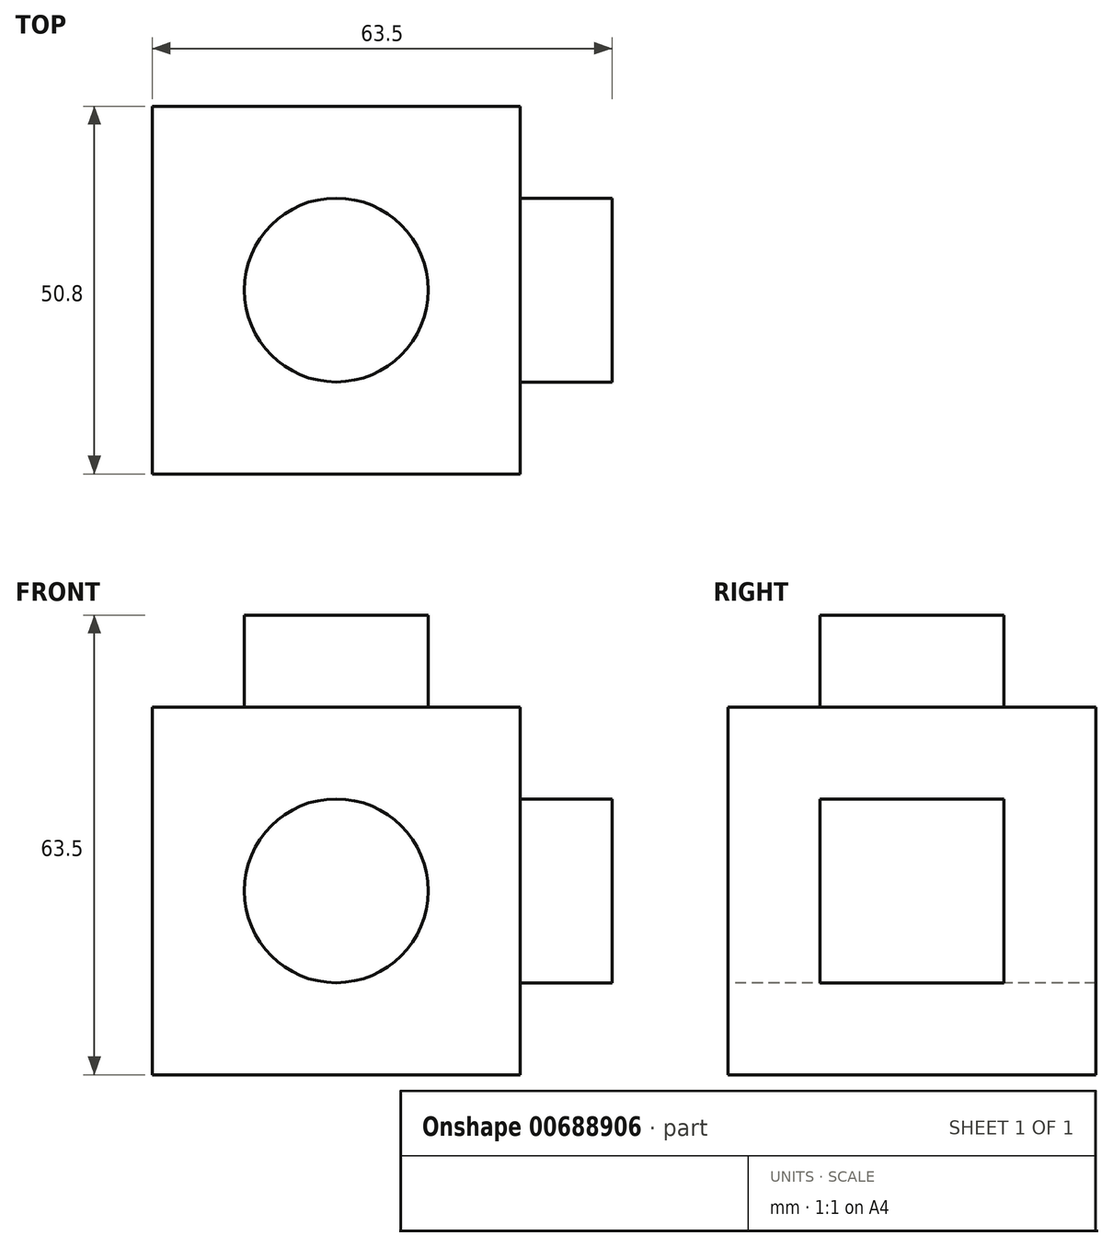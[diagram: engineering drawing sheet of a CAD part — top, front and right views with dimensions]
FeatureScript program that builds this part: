
annotation { "Feature Type Name" : "Feature", "Feature Type Description" : "" }
export const myFeature = defineFeature(function(context is Context, id is Id, definition is map)
    precondition{}
    {
        {
            var Q0;
            Q0=qCreatedBy(makeId("Front.planeOp"),FACE);
            var sketch = newSketch(context, id + "F0", { "sketchPlane" : qUnion([Q0])});
            skLineSegment(sketch, "E0.bottom", {"start": v(-18.43, 28.55) * mm, "end": v(32.37, 28.55) * mm});
            skLineSegment(sketch, "E0.top", {"start": v(-18.43, -22.25) * mm, "end": v(32.37, -22.25) * mm});
            skLineSegment(sketch, "E0.left", {"start": v(-18.43, 28.55) * mm, "end": v(-18.43, -22.25) * mm});
            skLineSegment(sketch, "E0.right", {"start": v(32.37, 28.55) * mm, "end": v(32.37, -22.25) * mm});
            skSolve(sketch);
        }
        {
            var Q0;
            Q0 = qSketchRegion(id + "F0", true);
            extrude(context, id + "F1", {"entities" : qUnion([Q0]), "depth" : 50.8 * mm, "offsetDistance" : 25.4 * mm});
        }
        {
            var Q0;
            Q0=makeQuery(id+"F1.opExtrude","CAP_FACE",FACE,{"disambiguationData":[OSD([sQuery(id+"F0.wireOp",EDGE,"E0.bottom"),sQuery(id+"F0.wireOp",EDGE,"E0.top"),sQuery(id+"F0.wireOp",EDGE,"E0.left"),sQuery(id+"F0.wireOp",EDGE,"E0.right")])],"isStart":false});
            var sketch = newSketch(context, id + "F2", { "sketchPlane" : qUnion([Q0])});
            skCircle(sketch, "E1", {"center": v(6.97, 3.15) * mm, "radius": 12.7 * mm});
            skSolve(sketch);
        }
        {
            var Q0;
            Q0 = qSketchRegion(id + "F2", true);
            extrude(context, id + "F3", {"entities" : qUnion([Q0]), "operationType" : NewBodyOperationType.REMOVE, "oppositeDirection" : true, "depth" : 50.8 * mm, "offsetDistance" : 25.4 * mm});
        }
        {
            var Q0;
            Q0=makeQuery(id+"F1.opExtrude","SWEPT_FACE",FACE,{"disambiguationData":[OSD([sQuery(id+"F0.wireOp",EDGE,"E0.right")])]});
            var sketch = newSketch(context, id + "F4", { "sketchPlane" : qUnion([Q0])});
            skLineSegment(sketch, "E2.bottom", {"start": v(-38.1, -9.55) * mm, "end": v(-12.7, -9.55) * mm});
            skLineSegment(sketch, "E2.top", {"start": v(-38.1, 15.85) * mm, "end": v(-12.7, 15.85) * mm});
            skLineSegment(sketch, "E2.left", {"start": v(-38.1, -9.55) * mm, "end": v(-38.1, 15.85) * mm});
            skLineSegment(sketch, "E2.right", {"start": v(-12.7, -9.55) * mm, "end": v(-12.7, 15.85) * mm});
            skSolve(sketch);
        }
        {
            var Q0;
            Q0 = qSketchRegion(id + "F4", true);
            extrude(context, id + "F5", {"entities" : qUnion([Q0]), "operationType" : NewBodyOperationType.ADD, "depth" : 12.7 * mm, "offsetDistance" : 25.4 * mm});
        }
        {
            var Q0;
            Q0=makeQuery(id+"F1.opExtrude","SWEPT_FACE",FACE,{"disambiguationData":[OSD([sQuery(id+"F0.wireOp",EDGE,"E0.bottom")])]});
            var sketch = newSketch(context, id + "F6", { "sketchPlane" : qUnion([Q0])});
            skCircle(sketch, "E3", {"center": v(6.97, -25.4) * mm, "radius": 12.7 * mm});
            skSolve(sketch);
        }
        {
            var Q0;
            Q0 = qSketchRegion(id + "F6", true);
            extrude(context, id + "F7", {"entities" : qUnion([Q0]), "operationType" : NewBodyOperationType.ADD, "depth" : 12.7 * mm, "offsetDistance" : 25.4 * mm});
        }
    });
